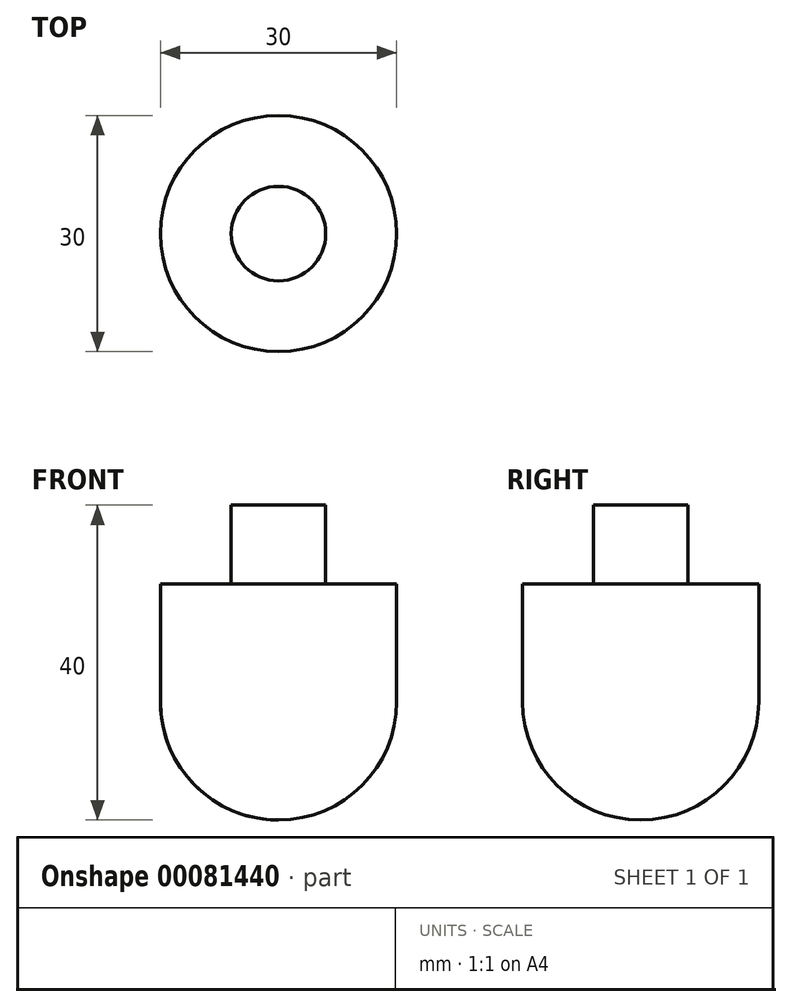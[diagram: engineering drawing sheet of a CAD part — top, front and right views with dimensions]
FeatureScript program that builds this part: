
annotation { "Feature Type Name" : "Feature", "Feature Type Description" : "" }
export const myFeature = defineFeature(function(context is Context, id is Id, definition is map)
    precondition{}
    {
        {
            var Q0;
            Q0=qCreatedBy(makeId("Front.planeOp"),FACE);
            var sketch = newSketch(context, id + "F0", { "sketchPlane" : qUnion([Q0])});
            skLineSegment(sketch, "E0.bottom", {"start": v(-6, 25) * mm, "end": v(6, 25) * mm});
            skLineSegment(sketch, "E0.top", {"start": v(-6, 15) * mm, "end": v(6, 15) * mm});
            skLineSegment(sketch, "E0.left", {"start": v(-6, 25) * mm, "end": v(-6, 15) * mm});
            skLineSegment(sketch, "E0.right", {"start": v(6, 25) * mm, "end": v(6, 15) * mm});
            skLineSegment(sketch, "E1.bottom", {"start": v(-15, 15) * mm, "end": v(15, 15) * mm});
            skLineSegment(sketch, "E1.top", {"start": v(-15, 0) * mm, "end": v(15, 0) * mm});
            skLineSegment(sketch, "E1.left", {"start": v(-15, 15) * mm, "end": v(-15, 0) * mm});
            skLineSegment(sketch, "E1.right", {"start": v(15, 15) * mm, "end": v(15, 0) * mm});
            skArc(sketch, "E2", {"start": v(-15, 0) * mm, "mid": v(0, -15) * mm, "end": v(15, 0) * mm});
            skLineSegment(sketch, "E3", {"start": v(0, 25) * mm, "end": v(0, -15) * mm});
            skSolve(sketch);
        }
        {
            var Q0;
            {var subQ0=sQuery(id+"F0.wireOp",EDGE,"E0.left");Q0=makeQuery(id+"F0.imprint","IMPRINT",FACE,{"disambiguationData":[TD([[makeQuery(id+"F0.imprint","IMPRINT",EDGE,{"derivedFrom":subQ0}),1.0]])]});}
            var Q1;
            {var subQ0=sQuery(id+"F0.wireOp",EDGE,"E1.left");Q1=makeQuery(id+"F0.imprint","IMPRINT",FACE,{"disambiguationData":[TD([[makeQuery(id+"F0.imprint","IMPRINT",EDGE,{"derivedFrom":subQ0}),1.0]])]});}
            var Q2;
            {var subQ0=sQuery(id+"F0.wireOp",EDGE,"E2");var subQ3=sQuery(id+"F0.wireOp",EDGE,"E3");var subQ5=makeQuery(id+"F0.imprint","INTERSECT",VERTEX,{"derivedFrom":[subQ0,subQ3]});Q2=makeQuery(id+"F0.imprint","IMPRINT",FACE,{"disambiguationData":[TD([[makeQuery(id+"F0.imprint","IMPRINT",EDGE,{"disambiguationData":[TD([[subQ5,1.0]])],"derivedFrom":subQ3}),-1.0]])]});}
            var Q3;
            Q3=sQuery(id+"F0.wireOp",EDGE,"E3");
            revolve(context, id + "F1", {"entities" : qUnion([Q0, Q1, Q2]), "axis" : qUnion([Q3]), "revolveType" : RevolveType.FULL});
        }
    });
